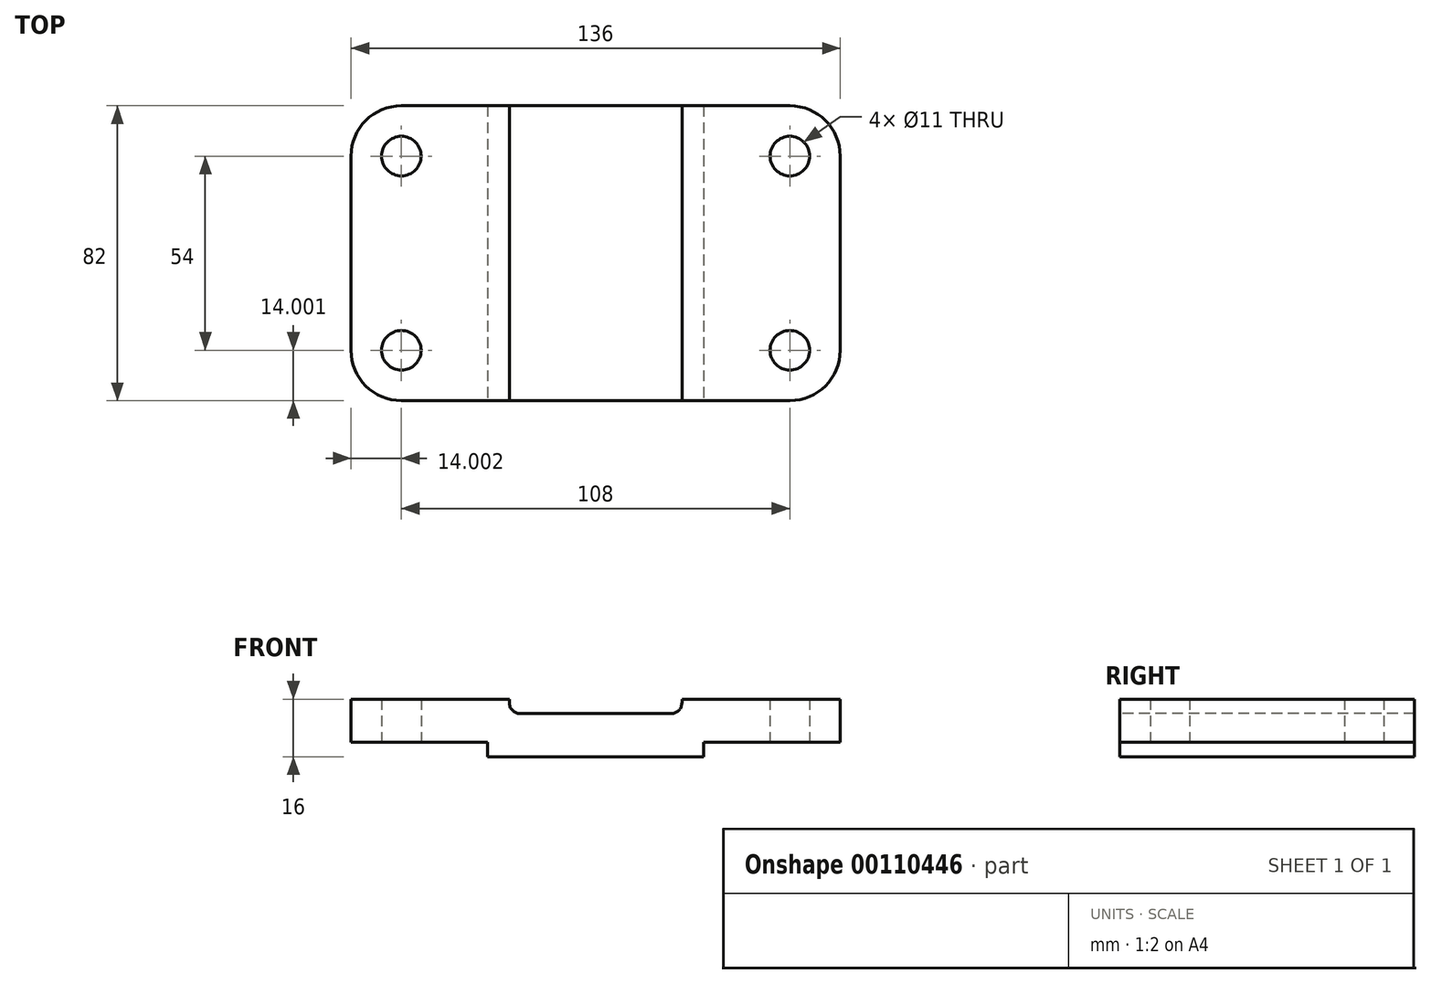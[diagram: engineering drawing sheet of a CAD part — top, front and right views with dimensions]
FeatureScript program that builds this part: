
annotation { "Feature Type Name" : "Feature", "Feature Type Description" : "" }
export const myFeature = defineFeature(function(context is Context, id is Id, definition is map)
    precondition{}
    {
        {
            var Q0;
            Q0=qCreatedBy(makeId("Top.planeOp"),FACE);
            var sketch = newSketch(context, id + "F0", { "sketchPlane" : qUnion([Q0])});
            skLineSegment(sketch, "E0.bottom", {"start": v(-50.46, 49.36) * mm, "end": v(57.54, 49.36) * mm});
            skLineSegment(sketch, "E0.top", {"start": v(-50.46, -32.64) * mm, "end": v(57.54, -32.64) * mm});
            skLineSegment(sketch, "E0.left", {"start": v(-64.46, 35.36) * mm, "end": v(-64.46, -18.64) * mm});
            skLineSegment(sketch, "E0.right", {"start": v(71.54, 35.36) * mm, "end": v(71.54, -18.64) * mm});
            skLineSegment(sketch, "E1.bottom", {"start": v(0, 23.9) * mm, "end": v(0, 23.9) * mm});
            skLineSegment(sketch, "E1.top", {"start": v(0, -21.63) * mm, "end": v(0, -21.63) * mm});
            skLineSegment(sketch, "E1.left", {"start": v(0, 23.9) * mm, "end": v(0, -21.63) * mm, "construction": true});
            skPoint(sketch, "E2.visualSharp", {"position": v(71.54, 49.36) * mm});
            skArc(sketch, "E2.filletArc", {"start": v(71.54, 35.36) * mm, "mid": v(67.44, 45.26) * mm, "end": v(57.54, 49.36) * mm});
            skPoint(sketch, "E3.visualSharp", {"position": v(-64.46, 49.36) * mm});
            skArc(sketch, "E3.filletArc", {"start": v(-50.46, 49.36) * mm, "mid": v(-60.36, 45.26) * mm, "end": v(-64.46, 35.36) * mm});
            skPoint(sketch, "E4.visualSharp", {"position": v(-64.46, -32.64) * mm});
            skArc(sketch, "E4.filletArc", {"start": v(-64.46, -18.64) * mm, "mid": v(-60.36, -28.54) * mm, "end": v(-50.46, -32.64) * mm});
            skPoint(sketch, "E5.visualSharp", {"position": v(71.54, -32.64) * mm});
            skArc(sketch, "E5.filletArc", {"start": v(57.54, -32.64) * mm, "mid": v(67.44, -28.54) * mm, "end": v(71.54, -18.64) * mm});
            skLineSegment(sketch, "E6", {"start": v(-25.43, 49.36) * mm, "end": v(-25.43, -32.64) * mm});
            skLineSegment(sketch, "E7", {"start": v(22.57, 49.36) * mm, "end": v(22.57, -32.64) * mm});
            skLineSegment(sketch, "E8", {"start": v(-75.5, 35.36) * mm, "end": v(71.54, 35.36) * mm, "construction": true});
            skLineSegment(sketch, "E9", {"start": v(-50.46, 49.36) * mm, "end": v(-50.46, -32.64) * mm, "construction": true});
            skLineSegment(sketch, "E10", {"start": v(57.54, 49.36) * mm, "end": v(57.54, -32.64) * mm, "construction": true});
            skCircle(sketch, "E11", {"center": v(57.54, 35.36) * mm, "radius": 5.5 * mm});
            skCircle(sketch, "E12", {"center": v(57.54, -18.64) * mm, "radius": 5.5 * mm});
            skCircle(sketch, "E13", {"center": v(-50.46, -18.64) * mm, "radius": 5.5 * mm});
            skCircle(sketch, "E14", {"center": v(-50.46, 35.36) * mm, "radius": 5.5 * mm});
            skSolve(sketch);
        }
        {
            var Q0;
            Q0 = qSketchRegion(id + "F0", true);
            extrude(context, id + "F1", {"entities" : qUnion([Q0]), "depth" : 16 * mm});
        }
        {
            var Q0;
            Q0=qCreatedBy(makeId("Front.planeOp"),FACE);
            var sketch = newSketch(context, id + "F2", { "sketchPlane" : qUnion([Q0])});
            skLineSegment(sketch, "E15.bottom", {"start": v(-64.46, 0) * mm, "end": v(-26.46, 0) * mm});
            skLineSegment(sketch, "E15.top", {"start": v(-64.46, 4) * mm, "end": v(-26.46, 4) * mm});
            skLineSegment(sketch, "E15.left", {"start": v(-64.46, 0) * mm, "end": v(-64.46, 4) * mm});
            skLineSegment(sketch, "E15.right", {"start": v(-26.46, 0) * mm, "end": v(-26.46, 4) * mm});
            skPoint(sketch, "E16.oppositeSnap0", {"position": v(-45.46, 4) * mm});
            skLineSegment(sketch, "E17", {"start": v(71.54, 0) * mm, "end": v(71.54, 4) * mm});
            skLineSegment(sketch, "E18", {"start": v(71.54, 4) * mm, "end": v(33.54, 4) * mm});
            skLineSegment(sketch, "E19", {"start": v(33.54, 4) * mm, "end": v(33.54, 0) * mm});
            skLineSegment(sketch, "E20", {"start": v(33.54, 0) * mm, "end": v(71.54, 0) * mm});
            skLineSegment(sketch, "E21", {"start": v(-64.46, 16.03) * mm, "end": v(-64.46, 22.42) * mm, "construction": true});
            skLineSegment(sketch, "E22", {"start": v(-64.46, 22.42) * mm, "end": v(-20.46, 22.42) * mm, "construction": true});
            skLineSegment(sketch, "E23", {"start": v(71.54, 16.03) * mm, "end": v(71.54, 22.68) * mm, "construction": true});
            skLineSegment(sketch, "E24", {"start": v(71.54, 22.68) * mm, "end": v(27.54, 22.68) * mm, "construction": true});
            skLineSegment(sketch, "E25.bottom", {"start": v(-20.46, 16) * mm, "end": v(27.54, 16) * mm});
            skLineSegment(sketch, "E25.top", {"start": v(-17.46, 12) * mm, "end": v(24.54, 12) * mm});
            skLineSegment(sketch, "E25.left", {"start": v(-20.46, 16) * mm, "end": v(-20.46, 15) * mm});
            skLineSegment(sketch, "E25.right", {"start": v(27.54, 16) * mm, "end": v(27.54, 15) * mm});
            skPoint(sketch, "E26.visualSharp", {"position": v(27.54, 12) * mm});
            skArc(sketch, "E26.filletArc", {"start": v(24.54, 12) * mm, "mid": v(26.66, 12.88) * mm, "end": v(27.54, 15) * mm});
            skPoint(sketch, "E27.visualSharp", {"position": v(-20.46, 12) * mm});
            skArc(sketch, "E27.filletArc", {"start": v(-20.46, 15) * mm, "mid": v(-19.58, 12.88) * mm, "end": v(-17.46, 12) * mm});
            skSolve(sketch);
        }
        {
            var Q0;
            Q0 = qSketchRegion(id + "F2", true);
            var Q1;
            Q1=makeQuery(id+"F1.opExtrude","SWEPT_FACE",FACE,{"disambiguationData":[OSD([sQuery(id+"F0.wireOp",EDGE,"E0.top")])]});
            extrude(context, id + "F3", {"entities" : qUnion([Q0]), "operationType" : NewBodyOperationType.REMOVE, "endBound" : BoundingType.THROUGH_ALL, "oppositeDirection" : true, "endBoundEntityFace" : qUnion([Q1]), "depth" : 25 * mm});
        }
        {
            var Q0;
            Q0 = qSketchRegion(id + "F2", true);
            extrude(context, id + "F4", {"entities" : qUnion([Q0]), "operationType" : NewBodyOperationType.REMOVE, "endBound" : BoundingType.THROUGH_ALL, "depth" : 25 * mm});
        }
    });
